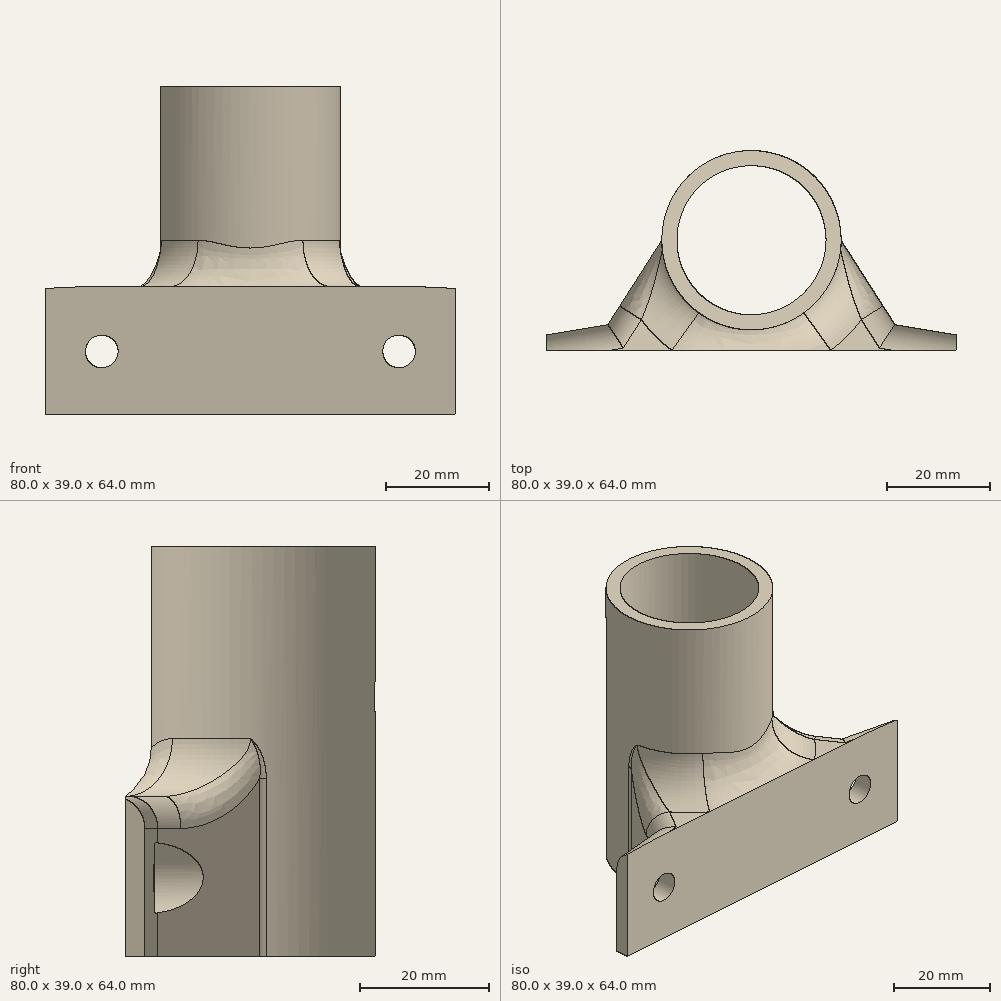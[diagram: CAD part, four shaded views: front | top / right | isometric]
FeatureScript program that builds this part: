
annotation { "Feature Type Name" : "Feature", "Feature Type Description" : "" }
export const myFeature = defineFeature(function(context is Context, id is Id, definition is map)
    precondition{}
    {
        {
            var Q0;
            Q0=qCreatedBy(makeId("Top.planeOp"),FACE);
            var sketch = newSketch(context, id + "F0", { "sketchPlane" : qUnion([Q0])});
            skCircle(sketch, "E0", {"center": v(0, 0) * mm, "radius": 14.55 * mm});
            skCircle(sketch, "E1", {"center": v(0, 0) * mm, "radius": 17.5 * mm});
            skSolve(sketch);
        }
        {
            var Q0;
            Q0 = qSketchRegion(id + "F0", true);
            extrude(context, id + "F1", {"entities" : qUnion([Q0]), "depth" : 64 * mm, "offsetDistance" : 25 * mm});
        }
        {
            var Q0;
            Q0=qCreatedBy(makeId("Top.planeOp"),FACE);
            var sketch = newSketch(context, id + "F2", { "sketchPlane" : qUnion([Q0])});
            skLineSegment(sketch, "E2.bottom", {"start": v(-17.45, 0) * mm, "end": v(-14.55, 0) * mm});
            skLineSegment(sketch, "E2.top", {"start": v(-40, -21.5) * mm, "end": v(0, -21.5) * mm});
            skLineSegment(sketch, "E2.left", {"start": v(-40, -18.5) * mm, "end": v(-40, -21.5) * mm});
            skLineSegment(sketch, "E3", {"start": v(-40, -18.5) * mm, "end": v(-28, -16.5) * mm});
            skLineSegment(sketch, "E4", {"start": v(-28, -16.5) * mm, "end": v(-17.45, 0) * mm});
            skPoint(sketch, "E5.orphan", {"position": v(40, -21.5) * mm});
            skLineSegment(sketch, "E6.MirrorCS", {"start": v(28, -16.5) * mm, "end": v(17.45, 0) * mm});
            skLineSegment(sketch, "E7.MirrorCS", {"start": v(17.45, 0) * mm, "end": v(14.55, 0) * mm});
            skLineSegment(sketch, "E8.MirrorCS", {"start": v(40, -18.5) * mm, "end": v(28, -16.5) * mm});
            skLineSegment(sketch, "E9.MirrorCS", {"start": v(40, -18.5) * mm, "end": v(40, -21.5) * mm});
            skLineSegment(sketch, "E10.MirrorCS", {"start": v(40, -21.5) * mm, "end": v(0, -21.5) * mm});
            skArc(sketch, "E11.0", {"start": v(-14.55, 0) * mm, "mid": v(0, -14.55) * mm, "end": v(14.55, 0) * mm});
            skSolve(sketch);
        }
        {
            var Q0;
            Q0 = qSketchRegion(id + "F2", true);
            extrude(context, id + "F3", {"entities" : qUnion([Q0]), "operationType" : NewBodyOperationType.ADD, "depth" : 25 * mm, "offsetDistance" : 25 * mm});
        }
        {
            var Q0;
            Q0=makeQuery(id+"F3.boolean.opBoolean","INTERSECT",EDGE,{"derivedFrom":[makeQuery(id+"F1.opExtrude","SWEPT_FACE",FACE,{"disambiguationData":[OSD([sQuery(id+"F0.wireOp",EDGE,"E1")])]}),makeQuery(id+"F3.opExtrude","CAP_FACE",FACE,{"disambiguationData":[OSD([sQuery(id+"F2.wireOp",EDGE,"E2.bottom"),sQuery(id+"F2.wireOp",EDGE,"E2.top"),sQuery(id+"F2.wireOp",EDGE,"E2.left"),sQuery(id+"F2.wireOp",EDGE,"E3"),sQuery(id+"F2.wireOp",EDGE,"E4"),sQuery(id+"F2.wireOp",EDGE,"E6.MirrorCS"),sQuery(id+"F2.wireOp",EDGE,"E7.MirrorCS"),sQuery(id+"F2.wireOp",EDGE,"E8.MirrorCS"),sQuery(id+"F2.wireOp",EDGE,"E9.MirrorCS"),sQuery(id+"F2.wireOp",EDGE,"E10.MirrorCS"),sQuery(id+"F2.wireOp",EDGE,"E11.0")])],"isStart":false})]});
            fillet(context, id + "F4", {"entities" : qUnion([Q0]), "radius" : 9 * mm, "tangentPropagation" : true, "allowEdgeOverflow" : false});
        }
        {
            var Q0;
            {var subQ0=sQuery(id+"F2.wireOp",EDGE,"E4");Q0=makeQuery(id+"F4.opFillet","BLEND_EDGE",EDGE,{"blendedFrom":[makeQuery(id+"F3.boolean.opBoolean","INTERSECT",EDGE,{"derivedFrom":[makeQuery(id+"F1.opExtrude","SWEPT_FACE",FACE,{"disambiguationData":[OSD([sQuery(id+"F0.wireOp",EDGE,"E1")])]}),makeQuery(id+"F3.opExtrude","CAP_FACE",FACE,{"disambiguationData":[OSD([sQuery(id+"F2.wireOp",EDGE,"E2.bottom"),sQuery(id+"F2.wireOp",EDGE,"E2.top"),sQuery(id+"F2.wireOp",EDGE,"E2.left"),sQuery(id+"F2.wireOp",EDGE,"E3"),subQ0,sQuery(id+"F2.wireOp",EDGE,"E6.MirrorCS"),sQuery(id+"F2.wireOp",EDGE,"E7.MirrorCS"),sQuery(id+"F2.wireOp",EDGE,"E8.MirrorCS"),sQuery(id+"F2.wireOp",EDGE,"E9.MirrorCS"),sQuery(id+"F2.wireOp",EDGE,"E10.MirrorCS"),sQuery(id+"F2.wireOp",EDGE,"E11.0")])],"isStart":false})]}),makeQuery(id+"F3.opExtrude","SWEPT_FACE",FACE,{"disambiguationData":[OSD([subQ0])]})],"blendedInto":[makeQuery(id+"F3.opExtrude","SWEPT_FACE",FACE,{"disambiguationData":[OSD([subQ0])]})]});}
            var Q1;
            Q1=makeQuery(id+"F3.opExtrude","CAP_EDGE",EDGE,{"disambiguationData":[OSD([sQuery(id+"F2.wireOp",EDGE,"E3")])],"isStart":false});
            var Q2;
            Q2=makeQuery(id+"F3.opExtrude","CAP_EDGE",EDGE,{"disambiguationData":[OSD([sQuery(id+"F2.wireOp",EDGE,"E6.MirrorCS")])],"isStart":false});
            var Q3;
            Q3=makeQuery(id+"F3.opExtrude","CAP_EDGE",EDGE,{"disambiguationData":[OSD([sQuery(id+"F2.wireOp",EDGE,"E8.MirrorCS")])],"isStart":false});
            fillet(context, id + "F5", {"entities" : qUnion([Q0, Q1, Q2, Q3]), "radius" : 5 * mm, "tangentPropagation" : true, "allowEdgeOverflow" : false});
        }
        {
            var Q0;
            Q0=makeQuery(id+"F3.opExtrude","SWEPT_FACE",FACE,{"disambiguationData":[OSD([sQuery(id+"F2.wireOp",EDGE,"E2.top"),sQuery(id+"F2.wireOp",EDGE,"E10.MirrorCS")])]});
            var sketch = newSketch(context, id + "F6", { "sketchPlane" : qUnion([Q0])});
            skLineSegment(sketch, "E12", {"start": v(-40, 12.28) * mm, "end": v(40, 12.28) * mm, "construction": true});
            skCircle(sketch, "E13", {"center": v(-29, 12.28) * mm, "radius": 3.17 * mm});
            skCircle(sketch, "E14", {"center": v(29, 12.28) * mm, "radius": 3.17 * mm});
            skLineSegment(sketch, "E15", {"start": v(-29, 12.28) * mm, "end": v(29, 12.28) * mm, "construction": true});
            skPoint(sketch, "E16", {"position": v(0, 12.28) * mm});
            skSolve(sketch);
        }
        {
            var Q0;
            Q0 = qSketchRegion(id + "F6", true);
            extrude(context, id + "F7", {"entities" : qUnion([Q0]), "operationType" : NewBodyOperationType.REMOVE, "endBound" : BoundingType.THROUGH_ALL, "oppositeDirection" : true, "depth" : 25 * mm, "offsetDistance" : 25 * mm});
        }
        {
            var Q0;
            Q0=makeQuery(id+"F3.opExtrude","SWEPT_FACE",FACE,{"disambiguationData":[OSD([sQuery(id+"F2.wireOp",EDGE,"E2.top"),sQuery(id+"F2.wireOp",EDGE,"E10.MirrorCS")])]});
            var sketch = newSketch(context, id + "F8", { "sketchPlane" : qUnion([Q0])});
            skCircle(sketch, "E17", {"center": v(-29, 12.28) * mm, "radius": 5.55 * mm});
            skCircle(sketch, "E18", {"center": v(29, 12.28) * mm, "radius": 5.55 * mm});
            skSolve(sketch);
        }
        {
            var Q0;
            Q0 = qSketchRegion(id + "F8", true);
            extrude(context, id + "F9", {"entities" : qUnion([Q0]), "operationType" : NewBodyOperationType.REMOVE, "oppositeDirection" : true, "depth" : 25 * mm, "offsetDistance" : 25 * mm, "hasSecondDirection" : true, "secondDirectionOppositeDirection" : true, "secondDirectionDepth" : 4.5 * mm});
        }
        {
            var Q0;
            Q0=qCreatedBy(makeId("Front.planeOp"),FACE);
            var sketch = newSketch(context, id + "F10", { "sketchPlane" : qUnion([Q0])});
            skCircle(sketch, "E19", {"center": v(0, 40.5) * mm, "radius": 2.67 * mm});
            skSolve(sketch);
        }
        {
            var Q0;
            Q0 = qSketchRegion(id + "F10", true);
            extrude(context, id + "F11", {"entities" : qUnion([Q0]), "operationType" : NewBodyOperationType.REMOVE, "endBound" : BoundingType.THROUGH_ALL, "oppositeDirection" : true, "depth" : 25 * mm, "offsetDistance" : 25 * mm});
        }
        {
            var Q0;
            Q0=makeQuery(id+"F3.boolean.opBoolean","INTERSECT",EDGE,{"derivedFrom":[makeQuery(id+"F1.opExtrude","SWEPT_FACE",FACE,{"disambiguationData":[OSD([sQuery(id+"F0.wireOp",EDGE,"E1")])]}),makeQuery(id+"F3.opExtrude","SWEPT_FACE",FACE,{"disambiguationData":[OSD([sQuery(id+"F2.wireOp",EDGE,"E4")])]})]});
            var Q1;
            {var subQ0=makeQuery(id+"F1.opExtrude","SWEPT_FACE",FACE,{"disambiguationData":[OSD([sQuery(id+"F0.wireOp",EDGE,"E1")])]});var subQ1=sQuery(id+"F2.wireOp",EDGE,"E4");Q1=makeQuery(id+"F5.opFillet","BLEND_EDGE",EDGE,{"blendedFrom":[makeQuery(id+"F4.opFillet","BLEND_EDGE",EDGE,{"blendedFrom":[makeQuery(id+"F3.boolean.opBoolean","INTERSECT",EDGE,{"derivedFrom":[subQ0,makeQuery(id+"F3.opExtrude","CAP_FACE",FACE,{"disambiguationData":[OSD([sQuery(id+"F2.wireOp",EDGE,"E2.bottom"),sQuery(id+"F2.wireOp",EDGE,"E2.top"),sQuery(id+"F2.wireOp",EDGE,"E2.left"),sQuery(id+"F2.wireOp",EDGE,"E3"),subQ1,sQuery(id+"F2.wireOp",EDGE,"E6.MirrorCS"),sQuery(id+"F2.wireOp",EDGE,"E7.MirrorCS"),sQuery(id+"F2.wireOp",EDGE,"E8.MirrorCS"),sQuery(id+"F2.wireOp",EDGE,"E9.MirrorCS"),sQuery(id+"F2.wireOp",EDGE,"E10.MirrorCS"),sQuery(id+"F2.wireOp",EDGE,"E11.0")])],"isStart":false})]}),makeQuery(id+"F3.opExtrude","SWEPT_FACE",FACE,{"disambiguationData":[OSD([subQ1])]})],"blendedInto":[makeQuery(id+"F3.opExtrude","SWEPT_FACE",FACE,{"disambiguationData":[OSD([subQ1])]})]}),subQ0],"blendedInto":[subQ0]});}
            var Q2;
            {var subQ0=makeQuery(id+"F1.opExtrude","SWEPT_FACE",FACE,{"disambiguationData":[OSD([sQuery(id+"F0.wireOp",EDGE,"E1")])]});Q2=makeQuery(id+"F4.opFillet","BLEND_EDGE",EDGE,{"disambiguationData":[OD(0.0)],"blendedFrom":[makeQuery(id+"F3.boolean.opBoolean","INTERSECT",EDGE,{"derivedFrom":[subQ0,makeQuery(id+"F3.opExtrude","CAP_FACE",FACE,{"disambiguationData":[OSD([sQuery(id+"F2.wireOp",EDGE,"E2.bottom"),sQuery(id+"F2.wireOp",EDGE,"E2.top"),sQuery(id+"F2.wireOp",EDGE,"E2.left"),sQuery(id+"F2.wireOp",EDGE,"E3"),sQuery(id+"F2.wireOp",EDGE,"E4"),sQuery(id+"F2.wireOp",EDGE,"E6.MirrorCS"),sQuery(id+"F2.wireOp",EDGE,"E7.MirrorCS"),sQuery(id+"F2.wireOp",EDGE,"E8.MirrorCS"),sQuery(id+"F2.wireOp",EDGE,"E9.MirrorCS"),sQuery(id+"F2.wireOp",EDGE,"E10.MirrorCS"),sQuery(id+"F2.wireOp",EDGE,"E11.0")])],"isStart":false})]}),subQ0],"blendedInto":[subQ0]});}
            var Q3;
            {var subQ0=makeQuery(id+"F1.opExtrude","SWEPT_FACE",FACE,{"disambiguationData":[OSD([sQuery(id+"F0.wireOp",EDGE,"E1")])]});Q3=makeQuery(id+"F4.opFillet","BLEND_EDGE",EDGE,{"disambiguationData":[OD(2.0)],"blendedFrom":[makeQuery(id+"F3.boolean.opBoolean","INTERSECT",EDGE,{"derivedFrom":[subQ0,makeQuery(id+"F3.opExtrude","CAP_FACE",FACE,{"disambiguationData":[OSD([sQuery(id+"F2.wireOp",EDGE,"E2.bottom"),sQuery(id+"F2.wireOp",EDGE,"E2.top"),sQuery(id+"F2.wireOp",EDGE,"E2.left"),sQuery(id+"F2.wireOp",EDGE,"E3"),sQuery(id+"F2.wireOp",EDGE,"E4"),sQuery(id+"F2.wireOp",EDGE,"E6.MirrorCS"),sQuery(id+"F2.wireOp",EDGE,"E7.MirrorCS"),sQuery(id+"F2.wireOp",EDGE,"E8.MirrorCS"),sQuery(id+"F2.wireOp",EDGE,"E9.MirrorCS"),sQuery(id+"F2.wireOp",EDGE,"E10.MirrorCS"),sQuery(id+"F2.wireOp",EDGE,"E11.0")])],"isStart":false})]}),subQ0],"blendedInto":[subQ0]});}
            var Q4;
            {var subQ0=makeQuery(id+"F1.opExtrude","SWEPT_FACE",FACE,{"disambiguationData":[OSD([sQuery(id+"F0.wireOp",EDGE,"E1")])]});Q4=makeQuery(id+"F4.opFillet","BLEND_EDGE",EDGE,{"disambiguationData":[OD(1.0)],"blendedFrom":[makeQuery(id+"F3.boolean.opBoolean","INTERSECT",EDGE,{"derivedFrom":[subQ0,makeQuery(id+"F3.opExtrude","CAP_FACE",FACE,{"disambiguationData":[OSD([sQuery(id+"F2.wireOp",EDGE,"E2.bottom"),sQuery(id+"F2.wireOp",EDGE,"E2.top"),sQuery(id+"F2.wireOp",EDGE,"E2.left"),sQuery(id+"F2.wireOp",EDGE,"E3"),sQuery(id+"F2.wireOp",EDGE,"E4"),sQuery(id+"F2.wireOp",EDGE,"E6.MirrorCS"),sQuery(id+"F2.wireOp",EDGE,"E7.MirrorCS"),sQuery(id+"F2.wireOp",EDGE,"E8.MirrorCS"),sQuery(id+"F2.wireOp",EDGE,"E9.MirrorCS"),sQuery(id+"F2.wireOp",EDGE,"E10.MirrorCS"),sQuery(id+"F2.wireOp",EDGE,"E11.0")])],"isStart":false})]}),subQ0],"blendedInto":[subQ0]});}
            var Q5;
            Q5=makeQuery(id+"F3.boolean.opBoolean","INTERSECT",EDGE,{"derivedFrom":[makeQuery(id+"F1.opExtrude","SWEPT_FACE",FACE,{"disambiguationData":[OSD([sQuery(id+"F0.wireOp",EDGE,"E1")])]}),makeQuery(id+"F3.opExtrude","SWEPT_FACE",FACE,{"disambiguationData":[OSD([sQuery(id+"F2.wireOp",EDGE,"E6.MirrorCS")])]})]});
            var Q6;
            {var subQ0=makeQuery(id+"F1.opExtrude","SWEPT_FACE",FACE,{"disambiguationData":[OSD([sQuery(id+"F0.wireOp",EDGE,"E1")])]});var subQ1=sQuery(id+"F2.wireOp",EDGE,"E6.MirrorCS");Q6=makeQuery(id+"F5.opFillet","BLEND_EDGE",EDGE,{"blendedFrom":[makeQuery(id+"F4.opFillet","BLEND_EDGE",EDGE,{"blendedFrom":[makeQuery(id+"F3.boolean.opBoolean","INTERSECT",EDGE,{"derivedFrom":[subQ0,makeQuery(id+"F3.opExtrude","CAP_FACE",FACE,{"disambiguationData":[OSD([sQuery(id+"F2.wireOp",EDGE,"E2.bottom"),sQuery(id+"F2.wireOp",EDGE,"E2.top"),sQuery(id+"F2.wireOp",EDGE,"E2.left"),sQuery(id+"F2.wireOp",EDGE,"E3"),sQuery(id+"F2.wireOp",EDGE,"E4"),subQ1,sQuery(id+"F2.wireOp",EDGE,"E7.MirrorCS"),sQuery(id+"F2.wireOp",EDGE,"E8.MirrorCS"),sQuery(id+"F2.wireOp",EDGE,"E9.MirrorCS"),sQuery(id+"F2.wireOp",EDGE,"E10.MirrorCS"),sQuery(id+"F2.wireOp",EDGE,"E11.0")])],"isStart":false})]}),makeQuery(id+"F3.opExtrude","SWEPT_FACE",FACE,{"disambiguationData":[OSD([subQ1])]})],"blendedInto":[makeQuery(id+"F3.opExtrude","SWEPT_FACE",FACE,{"disambiguationData":[OSD([subQ1])]})]}),subQ0],"blendedInto":[subQ0]});}
            fillet(context, id + "F12", {"entities" : qUnion([Q0, Q1, Q2, Q3, Q4, Q5, Q6]), "radius" : 2 * mm, "tangentPropagation" : true, "allowEdgeOverflow" : false});
        }
    });
